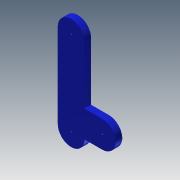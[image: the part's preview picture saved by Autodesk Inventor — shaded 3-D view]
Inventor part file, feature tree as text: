
AUTODESK INVENTOR PART (.ipt)
format: ipt  version: 2013 (Build 170138000, 138)  size: 132,608 bytes
history: native  units: mm
features: extrude x5, sketch x5
ambient origin geometry x8: Origin, YZ Plane, XZ Plane, XY Plane, X Axis, Y Axis, Z Axis, Center Point
bodies: Solid1 (feature_tree)
feature tree (10):
  extrude  "Extrusion1"  Depth=19.0mm
  extrude  "Extrusion2"  Depth=6.0mm
  extrude  "Extrusion3"  Depth=4.0mm
  extrude  "Extrusion4"  Depth=3.0mm
  extrude  "Extrusion5"  Depth=1.5mm TaperAngle=0.0deg
  sketch  "Sketch1"  dims[d0=6.0mm d1=19.0mm]
  sketch  "Sketch2"  dims[d2=6.0mm d4=6.0mm]
  sketch  "Sketch3"  dims[d5=4.0mm d6=4.0mm]
  sketch  "Sketch4"  dims[d7=2.0mm d10=3.0mm]
  sketch  "Sketch5"  dims[d11=6.0mm d12=1.5mm d13=0.0mm d14=3.0mm d15=3.0mm d16=4.0mm d17=6.0mm d18=1.5mm d19=0.0mm d20=4.0mm d21=6.0mm d22=4.0mm d23=1.5mm d24=0.0mm d25=3.0mm d26=1.5mm d27=0.0mm d28=0.2mm d29=0.2mm d30=0.2mm d31=1.5mm d32=0.0mm]
